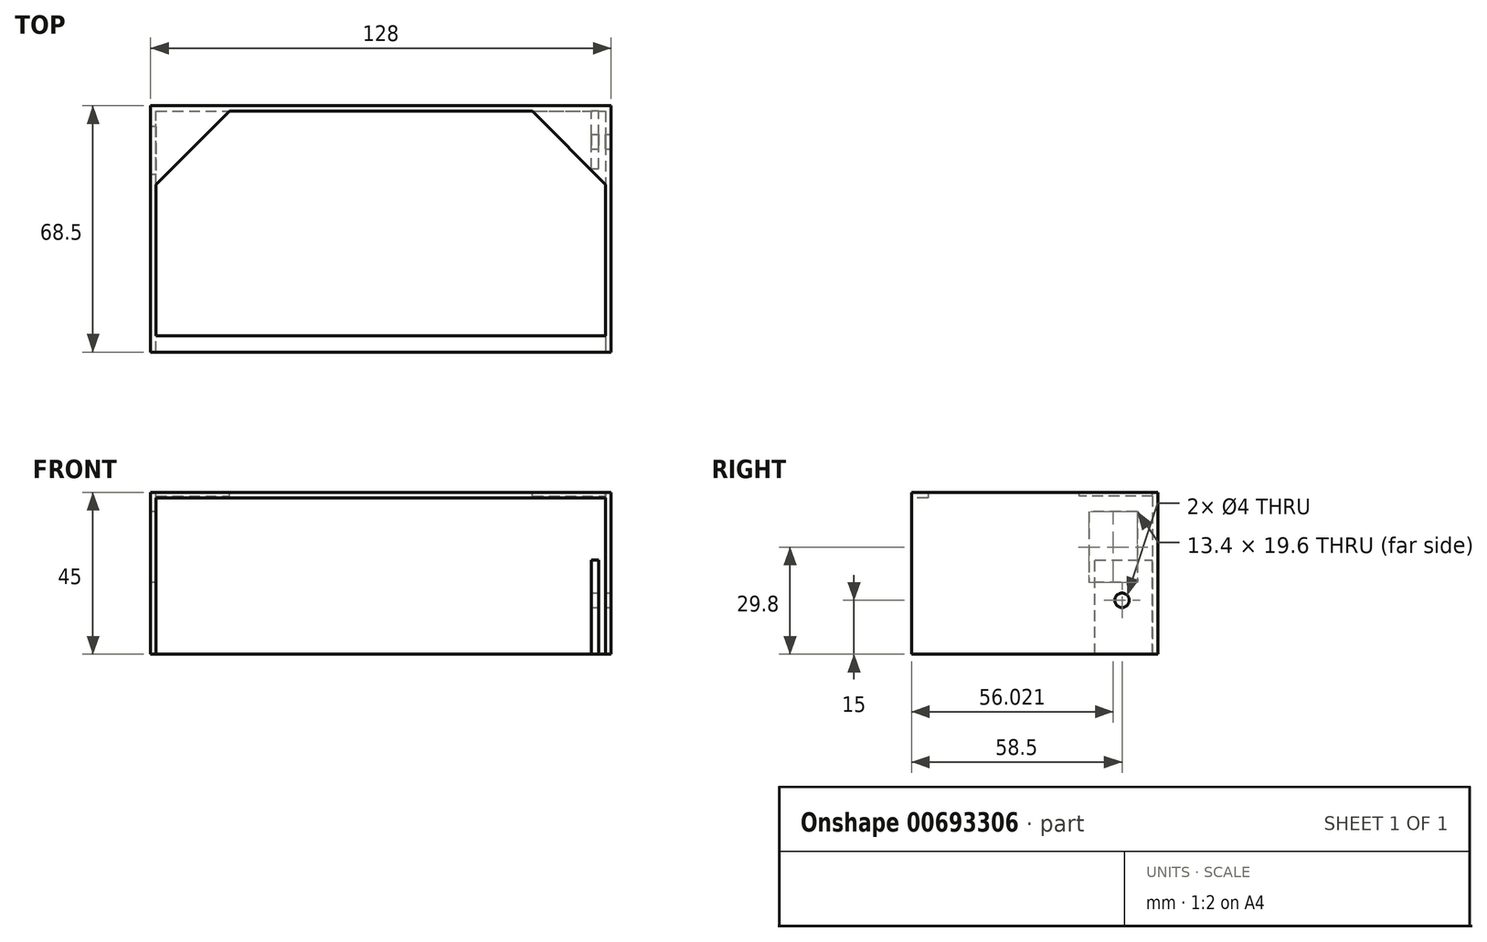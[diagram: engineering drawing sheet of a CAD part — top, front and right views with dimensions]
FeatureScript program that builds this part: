
annotation { "Feature Type Name" : "Feature", "Feature Type Description" : "" }
export const myFeature = defineFeature(function(context is Context, id is Id, definition is map)
    precondition{}
    {
        {
            var Q0;
            Q0=qCreatedBy(makeId("Top.planeOp"),FACE);
            var sketch = newSketch(context, id + "F0", { "sketchPlane" : qUnion([Q0])});
            skLineSegment(sketch, "E0", {"start": v(-62.5, 0) * mm, "end": v(-62.5, 67) * mm});
            skLineSegment(sketch, "E1", {"start": v(62.5, 67) * mm, "end": v(62.5, 0) * mm});
            skLineSegment(sketch, "E2", {"start": v(-62.5, 67) * mm, "end": v(62.5, 67) * mm});
            skLineSegment(sketch, "E3.0", {"start": v(64, 68.5) * mm, "end": v(64, 0) * mm});
            skLineSegment(sketch, "E3.1", {"start": v(-64, 68.5) * mm, "end": v(64, 68.5) * mm});
            skLineSegment(sketch, "E3.2", {"start": v(-64, 0) * mm, "end": v(-64, 68.5) * mm});
            skLineSegment(sketch, "E4", {"start": v(64, 0) * mm, "end": v(62.5, 0) * mm});
            skLineSegment(sketch, "E5", {"start": v(-64, 0) * mm, "end": v(-62.5, 0) * mm});
            skSolve(sketch);
        }
        {
            var Q0;
            Q0=makeQuery(id+"F0.imprint","IMPRINT",FACE,{"disambiguationData":[TD([[makeQuery(id+"F0.imprint","IMPRINT",EDGE,{"derivedFrom":sQuery(id+"F0.wireOp",EDGE,"E0")}),1.0]])]});
            extrude(context, id + "F1", {"entities" : qUnion([Q0]), "depth" : 45 * mm, "offsetDistance" : 25 * mm});
        }
        {
            var Q0;
            Q0=makeQuery(id+"F1.opExtrude","SWEPT_FACE",FACE,{"disambiguationData":[OSD([sQuery(id+"F0.wireOp",EDGE,"E3.2")])]});
            var sketch = newSketch(context, id + "F2", { "sketchPlane" : qUnion([Q0])});
            skLineSegment(sketch, "E6.bottom", {"start": v(-62.72, 39.6) * mm, "end": v(-49.32, 39.6) * mm});
            skLineSegment(sketch, "E6.top", {"start": v(-62.72, 20) * mm, "end": v(-49.32, 20) * mm});
            skLineSegment(sketch, "E6.left", {"start": v(-62.72, 39.6) * mm, "end": v(-62.72, 20) * mm});
            skLineSegment(sketch, "E6.right", {"start": v(-49.32, 39.6) * mm, "end": v(-49.32, 20) * mm});
            skSolve(sketch);
        }
        {
            var Q0;
            Q0=makeQuery(id+"F2.imprint","IMPRINT",FACE,{"disambiguationData":[TD([[makeQuery(id+"F2.imprint","IMPRINT",EDGE,{"derivedFrom":sQuery(id+"F2.wireOp",EDGE,"E6.bottom")}),-1.0]])]});
            extrude(context, id + "F3", {"entities" : qUnion([Q0]), "operationType" : NewBodyOperationType.REMOVE, "endBound" : BoundingType.SYMMETRIC, "oppositeDirection" : true, "depth" : 6 * mm, "offsetDistance" : 25 * mm});
        }
        {
            var Q0;
            Q0=makeQuery(id+"F1.opExtrude","CAP_FACE",FACE,{"disambiguationData":[OSD([sQuery(id+"F0.wireOp",EDGE,"E0"),sQuery(id+"F0.wireOp",EDGE,"E1"),sQuery(id+"F0.wireOp",EDGE,"E2"),sQuery(id+"F0.wireOp",EDGE,"E3.0"),sQuery(id+"F0.wireOp",EDGE,"E3.1"),sQuery(id+"F0.wireOp",EDGE,"E3.2"),sQuery(id+"F0.wireOp",EDGE,"E4"),sQuery(id+"F0.wireOp",EDGE,"E5")])],"isStart":false});
            var sketch = newSketch(context, id + "F4", { "sketchPlane" : qUnion([Q0])});
            skLineSegment(sketch, "E7", {"start": v(-62.5, 67) * mm, "end": v(-62.5, 46.62) * mm});
            skLineSegment(sketch, "E8", {"start": v(-62.5, 46.62) * mm, "end": v(-42.12, 67) * mm});
            skLineSegment(sketch, "E9", {"start": v(-42.12, 67) * mm, "end": v(-62.5, 67) * mm});
            skLineSegment(sketch, "E10.MirrorCS", {"start": v(42.12, 67) * mm, "end": v(62.5, 67) * mm});
            skLineSegment(sketch, "E11.MirrorCS", {"start": v(62.5, 67) * mm, "end": v(62.5, 46.62) * mm});
            skLineSegment(sketch, "E12.MirrorCS", {"start": v(62.5, 46.62) * mm, "end": v(42.12, 67) * mm});
            skSolve(sketch);
        }
        {
            var Q0;
            Q0=makeQuery(id+"F4.imprint","IMPRINT",FACE,{"disambiguationData":[TD([[makeQuery(id+"F4.imprint","IMPRINT",EDGE,{"derivedFrom":sQuery(id+"F4.wireOp",EDGE,"E7")}),-1.0]])]});
            var Q1;
            Q1=makeQuery(id+"F4.imprint","IMPRINT",FACE,{"disambiguationData":[TD([[makeQuery(id+"F4.imprint","IMPRINT",EDGE,{"derivedFrom":sQuery(id+"F4.wireOp",EDGE,"E10.MirrorCS")}),-1.0]])]});
            extrude(context, id + "F5", {"entities" : qUnion([Q0, Q1]), "operationType" : NewBodyOperationType.ADD, "oppositeDirection" : true, "depth" : 1 * mm, "offsetDistance" : 25 * mm});
        }
        {
            var Q0;
            Q0=makeQuery(id+"F1.opExtrude","SWEPT_FACE",FACE,{"disambiguationData":[OSD([sQuery(id+"F0.wireOp",EDGE,"E3.0")])]});
            var sketch = newSketch(context, id + "F6", { "sketchPlane" : qUnion([Q0])});
            skCircle(sketch, "E13", {"center": v(58.5, 15) * mm, "radius": 2 * mm});
            skSolve(sketch);
        }
        {
            var Q0;
            {var subQ10=sQuery(id+"F4.wireOp",EDGE,"E7");Q0=makeQuery(id+"F4.imprint","IMPRINT",FACE,{"disambiguationData":[TD([[makeQuery(id+"F4.imprint","IMPRINT",EDGE,{"derivedFrom":subQ10}),1.0]])]});}
            var sketch = newSketch(context, id + "F7", { "sketchPlane" : qUnion([Q0])});
            skLineSegment(sketch, "E14.bottom", {"start": v(-62.63, 0) * mm, "end": v(62.98, 0) * mm});
            skLineSegment(sketch, "E14.top", {"start": v(-62.63, 4.58) * mm, "end": v(62.98, 4.58) * mm});
            skLineSegment(sketch, "E14.left", {"start": v(-62.63, 0) * mm, "end": v(-62.63, 4.58) * mm});
            skLineSegment(sketch, "E14.right", {"start": v(62.98, 0) * mm, "end": v(62.98, 4.58) * mm});
            skSolve(sketch);
        }
        {
            var Q0;
            Q0 = qSketchRegion(id + "F7", true);
            extrude(context, id + "F8", {"entities" : qUnion([Q0]), "operationType" : NewBodyOperationType.ADD, "oppositeDirection" : true, "depth" : 1.5 * mm, "offsetDistance" : 25 * mm});
        }
        {
            var Q0;
            Q0=makeQuery(id+"F1.opExtrude","SWEPT_FACE",FACE,{"disambiguationData":[OSD([sQuery(id+"F0.wireOp",EDGE,"E2")])]});
            var sketch = newSketch(context, id + "F9", { "sketchPlane" : qUnion([Q0])});
            skLineSegment(sketch, "E15.bottom", {"start": v(60.5, 0) * mm, "end": v(58.51, 0) * mm});
            skLineSegment(sketch, "E15.top", {"start": v(60.5, 26.2) * mm, "end": v(58.51, 26.2) * mm});
            skLineSegment(sketch, "E15.left", {"start": v(60.5, 0) * mm, "end": v(60.5, 26.2) * mm});
            skLineSegment(sketch, "E15.right", {"start": v(58.51, 0) * mm, "end": v(58.51, 26.2) * mm});
            skSolve(sketch);
        }
        {
            var Q0;
            Q0 = qSketchRegion(id + "F9", true);
            extrude(context, id + "F10", {"entities" : qUnion([Q0]), "operationType" : NewBodyOperationType.ADD, "depth" : 16 * mm, "offsetDistance" : 25 * mm});
        }
        {
            var Q0;
            Q0=makeQuery(id+"F6.imprint","IMPRINT",FACE,{"disambiguationData":[TD([[makeQuery(id+"F6.imprint","IMPRINT",EDGE,{"derivedFrom":sQuery(id+"F6.wireOp",EDGE,"E13")}),1.0]])]});
            extrude(context, id + "F11", {"entities" : qUnion([Q0]), "operationType" : NewBodyOperationType.REMOVE, "endBound" : BoundingType.SYMMETRIC, "oppositeDirection" : true, "depth" : 18.8 * mm, "offsetDistance" : 25 * mm});
        }
    });
